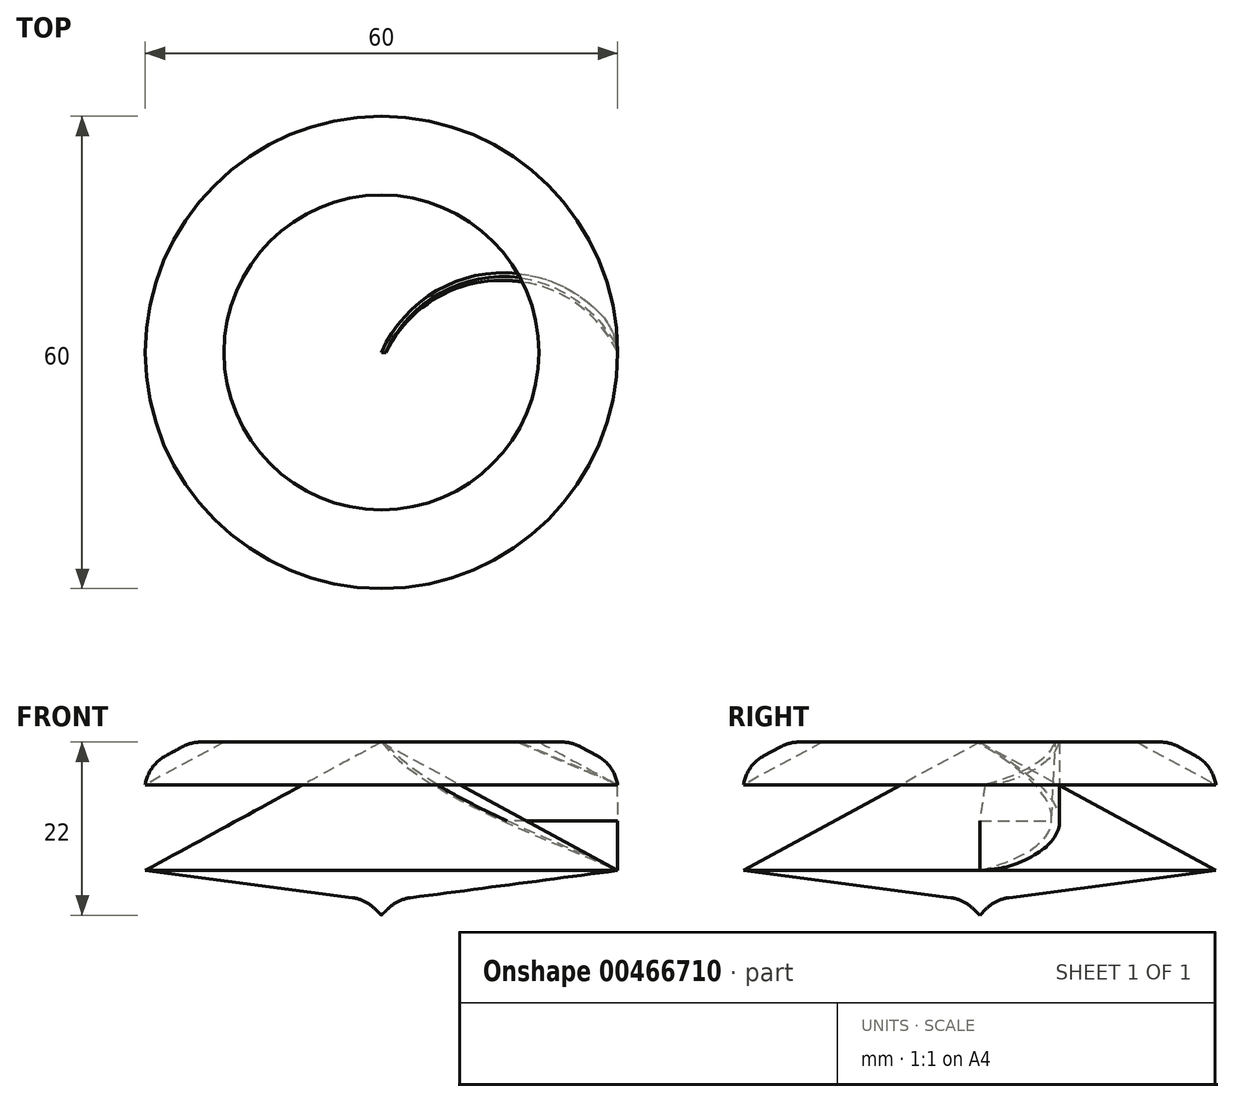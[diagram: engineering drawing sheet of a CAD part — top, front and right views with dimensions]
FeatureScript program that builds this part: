
annotation { "Feature Type Name" : "Feature", "Feature Type Description" : "" }
export const myFeature = defineFeature(function(context is Context, id is Id, definition is map)
    precondition{}
    {
        {
            var Q0;
            Q0=qCreatedBy(makeId("Top.planeOp"),FACE);
            var sketch = newSketch(context, id + "F0", { "sketchPlane" : qUnion([Q0])});
            skCircle(sketch, "E0", {"center": v(0, 0) * mm, "radius": 30 * mm});
            skArc(sketch, "E1", {"start": v(30, 0) * mm, "mid": v(15.55, 9.13) * mm, "end": v(1.1, 0) * mm});
            skArc(sketch, "E2.0", {"start": v(29.92, 2.22) * mm, "mid": v(14.3, 10.08) * mm, "end": v(0, 0) * mm});
            skLineSegment(sketch, "E3", {"start": v(0, 0) * mm, "end": v(1.1, 0) * mm});
            skSolve(sketch);
        }
        {
            var Q0;
            {var subQ0=sQuery(id+"F0.wireOp",EDGE,"E1");Q0=makeQuery(id+"F0.imprint","IMPRINT",FACE,{"disambiguationData":[TD([[makeQuery(id+"F0.imprint","IMPRINT",EDGE,{"derivedFrom":subQ0}),-1.0]])]});}
            extrude(context, id + "F1", {"entities" : qUnion([Q0]), "depth" : 22 * mm});
        }
        {
            var Q0;
            Q0=makeQuery(id+"F1.opExtrude","SWEPT_EDGE",EDGE,{"disambiguationData":[OSD([sQuery(id+"F0.wireOp",EDGE,"E0"),sQuery(id+"F0.wireOp",EDGE,"E2.0")])]});
            fillet(context, id + "F2", {"entities" : qUnion([Q0]), "radius" : 8 * mm, "tangentPropagation" : true, "allowEdgeOverflow" : false});
        }
        {
            var Q0;
            Q0=makeQuery(id+"F1.opExtrude","CAP_EDGE",EDGE,{"disambiguationData":[OSD([sQuery(id+"F0.wireOp",EDGE,"E1")])],"isStart":false});
            chamfer(context, id + "F3", {"entities" : qUnion([Q0]), "chamferType" : ChamferType.TWO_OFFSETS, "width1" : 10 * mm, "oppositeDirection" : false, "width2" : .5 * mm, "tangentPropagation" : true});
        }
        {
            var Q0;
            Q0=qCreatedBy(makeId("Right.planeOp"),FACE);
            var sketch = newSketch(context, id + "F4", { "sketchPlane" : qUnion([Q0])});
            skLineSegment(sketch, "E4.0", {"start": v(-30, 0) * mm, "end": v(30, 0) * mm, "construction": true});
            skLineSegment(sketch, "E5", {"start": v(0, 22) * mm, "end": v(-30, 22) * mm, "construction": true});
            skLineSegment(sketch, "E6", {"start": v(-30, 5.69) * mm, "end": v(0, 22) * mm});
            skLineSegment(sketch, "E7", {"start": v(-30, 22) * mm, "end": v(-20, 22) * mm});
            skLineSegment(sketch, "E8", {"start": v(-20, 22) * mm, "end": v(-30, 16.56) * mm});
            skLineSegment(sketch, "E9", {"start": v(-24.19, 22) * mm, "end": v(-30, 18.84) * mm});
            skLineSegment(sketch, "E10.0", {"start": v(0, 22) * mm, "end": v(0, 0) * mm, "construction": true});
            skLineSegment(sketch, "E11", {"start": v(0, 0) * mm, "end": v(0, 0) * mm});
            skLineSegment(sketch, "E12", {"start": v(0, 22) * mm, "end": v(0, 0) * mm});
            skLineSegment(sketch, "E13", {"start": v(-20, 22) * mm, "end": v(0, 22) * mm});
            skLineSegment(sketch, "E14", {"start": v(-30, 0) * mm, "end": v(0, 0) * mm});
            skLineSegment(sketch, "E15", {"start": v(-30, 22) * mm, "end": v(-30, 0) * mm});
            skLineSegment(sketch, "E16", {"start": v(-30, 5.69) * mm, "end": v(-2, 2) * mm});
            skLineSegment(sketch, "E17", {"start": v(-2, 2) * mm, "end": v(0, 0) * mm});
            skSolve(sketch);
        }
        {
            var Q0;
            Q0=makeQuery(id+"F4.imprint","IMPRINT",FACE,{"disambiguationData":[TD([[makeQuery(id+"F4.imprint","IMPRINT",EDGE,{"derivedFrom":sQuery(id+"F4.wireOp",EDGE,"E6")}),-1.0]])]});
            var Q1;
            {var subQ0=sQuery(id+"F4.wireOp",EDGE,"E14");Q1=makeQuery(id+"F4.imprint","IMPRINT",FACE,{"disambiguationData":[TD([[makeQuery(id+"F4.imprint","IMPRINT",EDGE,{"derivedFrom":subQ0}),1.0]])]});}
            var Q2;
            {var subQ0=sQuery(id+"F4.wireOp",EDGE,"E8");Q2=makeQuery(id+"F4.imprint","IMPRINT",FACE,{"disambiguationData":[TD([[makeQuery(id+"F4.imprint","IMPRINT",EDGE,{"derivedFrom":subQ0}),-1.0]])]});}
            var Q3;
            {var subQ3=sQuery(id+"F4.wireOp",EDGE,"E9");Q3=makeQuery(id+"F4.imprint","IMPRINT",FACE,{"disambiguationData":[TD([[makeQuery(id+"F4.imprint","IMPRINT",EDGE,{"derivedFrom":subQ3}),-1.0]])]});}
            var Q4;
            Q4=sQuery(id+"F4.wireOp",EDGE,"E12");
            revolve(context, id + "F5", {"operationType" : NewBodyOperationType.REMOVE, "entities" : qUnion([Q0, Q1, Q2, Q3]), "axis" : qUnion([Q4]), "revolveType" : RevolveType.FULL, "oppositeDirection" : true});
        }
        {
            var Q0;
            Q0=makeQuery(id+"F4.imprint","IMPRINT",FACE,{"disambiguationData":[TD([[makeQuery(id+"F4.imprint","IMPRINT",EDGE,{"derivedFrom":sQuery(id+"F4.wireOp",EDGE,"E6")}),-1.0]])]});
            var Q1;
            {var subQ0=sQuery(id+"F4.wireOp",EDGE,"E8");Q1=makeQuery(id+"F4.imprint","IMPRINT",FACE,{"disambiguationData":[TD([[makeQuery(id+"F4.imprint","IMPRINT",EDGE,{"derivedFrom":subQ0}),-1.0]])]});}
            var Q2;
            Q2=sQuery(id+"F4.wireOp",EDGE,"E12");
            revolve(context, id + "F6", {"entities" : qUnion([Q0, Q1]), "axis" : qUnion([Q2]), "revolveType" : RevolveType.FULL});
        }
        {
            var Q0;
            Q0=makeQuery(id+"F6.opRevolve","SWEPT_EDGE",EDGE,{"disambiguationData":[OSD([sQuery(id+"F4.wireOp",EDGE,"E7"),sQuery(id+"F4.wireOp",EDGE,"E9")])]});
            var Q1;
            Q1=makeQuery(id+"F6.opRevolve","SWEPT_EDGE",EDGE,{"disambiguationData":[OSD([sQuery(id+"F4.wireOp",EDGE,"E9"),sQuery(id+"F4.wireOp",EDGE,"E15")])]});
            var Q2;
            Q2=makeQuery(id+"F6.opRevolve","SWEPT_EDGE",EDGE,{"disambiguationData":[OSD([sQuery(id+"F4.wireOp",EDGE,"E16"),sQuery(id+"F4.wireOp",EDGE,"E17")])]});
            fillet(context, id + "F7", {"entities" : qUnion([Q0, Q1, Q2]), "radius" : 5 * mm, "tangentPropagation" : true, "allowEdgeOverflow" : false});
        }
    });
